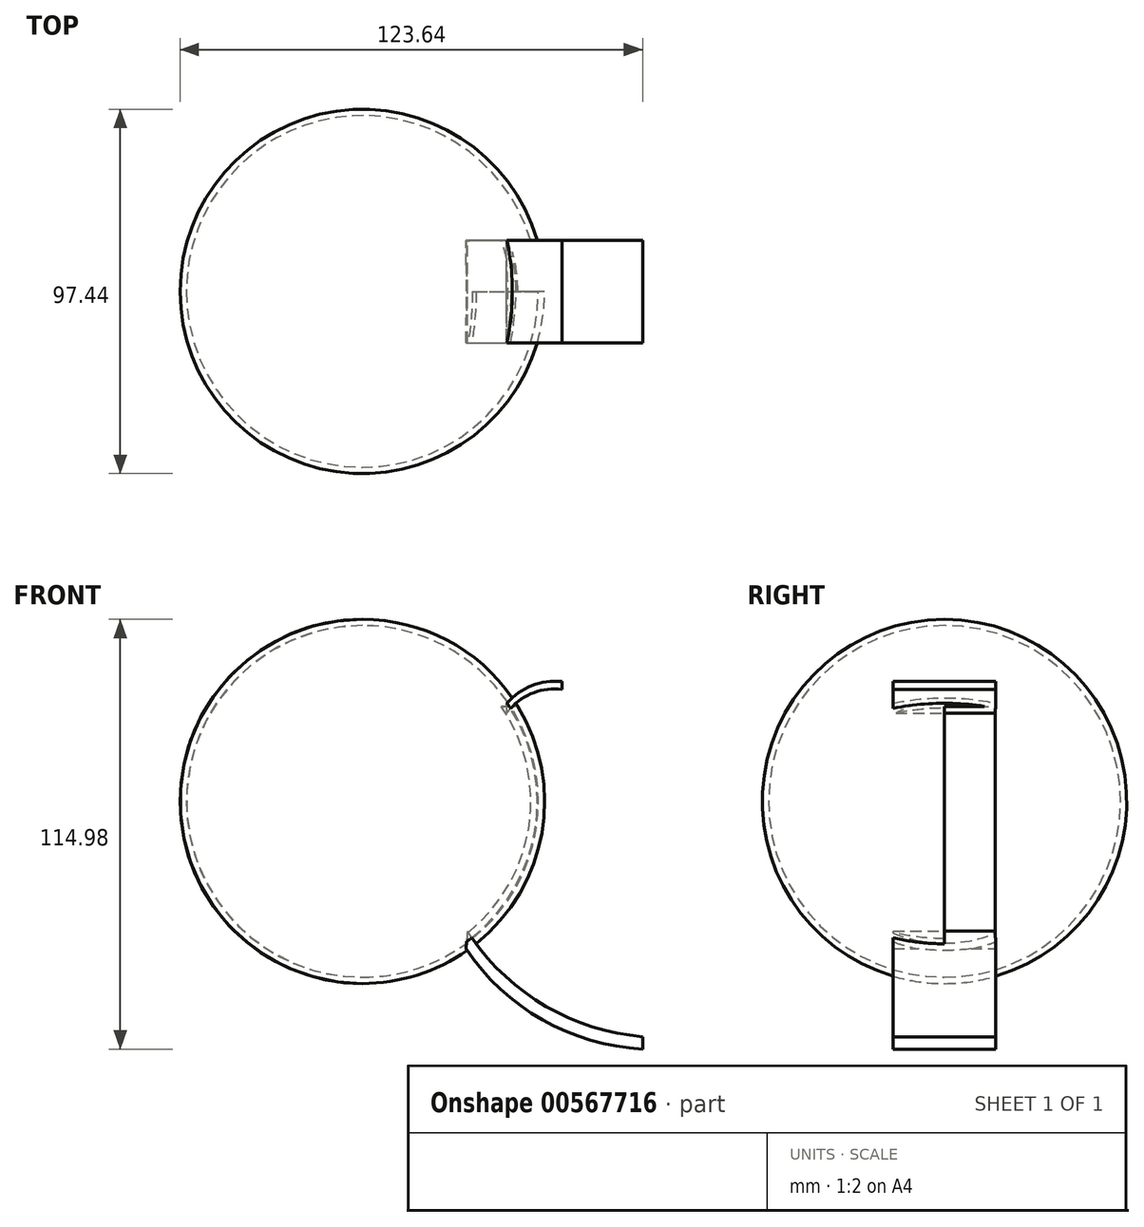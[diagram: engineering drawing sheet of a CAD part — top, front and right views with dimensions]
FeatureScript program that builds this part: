
annotation { "Feature Type Name" : "Feature", "Feature Type Description" : "" }
export const myFeature = defineFeature(function(context is Context, id is Id, definition is map)
    precondition{}
    {
        {
            var Q0;
            Q0=qCreatedBy(makeId("Front.planeOp"),FACE);
            var sketch = newSketch(context, id + "F0", { "sketchPlane" : qUnion([Q0])});
            skLineSegment(sketch, "E0", {"start": v(0, 0) * mm, "end": v(0, 97.44) * mm});
            skArc(sketch, "E1", {"start": v(0, 0) * mm, "mid": v(48.72, 48.72) * mm, "end": v(0, 97.44) * mm});
            skArc(sketch, "E2", {"start": v(0, 4.64) * mm, "mid": v(-1.9, 4.69) * mm, "end": v(-3.78, 4.8) * mm});
            skArc(sketch, "E3", {"start": v(0, 1.68) * mm, "mid": v(47.04, 48.72) * mm, "end": v(0, 95.76) * mm});
            skSolve(sketch);
        }
        {
            var Q0;
            {var subQ0=sQuery(id+"F0.wireOp",EDGE,"E1");Q0=makeQuery(id+"F0.imprint","IMPRINT",FACE,{"disambiguationData":[TD([[makeQuery(id+"F0.imprint","IMPRINT",EDGE,{"derivedFrom":subQ0}),1.0]])]});}
            var Q1;
            Q1=sQuery(id+"F0.wireOp",EDGE,"E0");
            revolve(context, id + "F1", {"entities" : qUnion([Q0]), "axis" : qUnion([Q1]), "revolveType" : RevolveType.ONE_DIRECTION, "angle" : 180 * degree});
        }
        {
            var Q0;
            Q0=makeQuery(id+"F1.opRevolve","SWEPT_BODY",BODY,{"disambiguationData":[OSD([sQuery(id+"F0.wireOp",EDGE,"E0"),sQuery(id+"F0.wireOp",EDGE,"E1"),sQuery(id+"F0.wireOp",EDGE,"E3")])]});
            var Q1;
            Q1=qCreatedBy(makeId("Front.planeOp"),FACE);
            mirror(context, id + "F2", {"operationType" : NewBodyOperationType.ADD, "entities" : qUnion([Q0]), "mirrorPlane" : qUnion([Q1])});
        }
        {
            var Q0;
            Q0=qCreatedBy(makeId("Top.planeOp"),FACE);
            var sketch = newSketch(context, id + "F3", { "sketchPlane" : qUnion([Q0])});
            skLineSegment(sketch, "E4", {"start": v(28.32, 0) * mm, "end": v(28.32, 13.61) * mm});
            skLineSegment(sketch, "E5", {"start": v(28.32, 13.61) * mm, "end": v(62.18, 13.61) * mm});
            skLineSegment(sketch, "E6", {"start": v(62.18, 13.61) * mm, "end": v(62.18, 0) * mm});
            skLineSegment(sketch, "E7", {"start": v(62.18, 0) * mm, "end": v(28.32, 0) * mm});
            skSolve(sketch);
        }
        {
            var Q0;
            Q0=makeQuery(id+"Fv1a8QCHK5ZU15p_1.1.F3.imprint","IMPRINT",FACE,{"disambiguationData":[TD([[makeQuery(id+"Fv1a8QCHK5ZU15p_1.1.F3.imprint","IMPRINT",EDGE,{"derivedFrom":sQuery(id+"Fv1a8QCHK5ZU15p_1.1.F3.wireOp",EDGE,"E4")}),-1.0]])]});
            var Q1;
            Q1=makeQuery(id+"F3.imprint","IMPRINT",FACE,{"disambiguationData":[TD([[makeQuery(id+"F3.imprint","IMPRINT",EDGE,{"derivedFrom":sQuery(id+"F3.wireOp",EDGE,"E4")}),-1.0]])]});
            extrude(context, id + "F4", {"entities" : qUnion([Q0, Q1]), "operationType" : NewBodyOperationType.REMOVE, "depth" : 74.17 * mm, "offsetDistance" : 25.4 * mm});
        }
        {
            var Q0;
            Q0=qCreatedBy(makeId("Front.planeOp"),FACE);
            var sketch = newSketch(context, id + "F5", { "sketchPlane" : qUnion([Q0])});
            skArc(sketch, "E8", {"start": v(28.06, 14) * mm, "mid": v(48.2, -5.57) * mm, "end": v(74.92, -14.22) * mm});
            skArc(sketch, "E9", {"start": v(27.72, 9.28) * mm, "mid": v(48.15, -9.72) * mm, "end": v(74.92, -17.54) * mm});
            skLineSegment(sketch, "E10", {"start": v(28.06, 14) * mm, "end": v(27.72, 9.28) * mm});
            skLineSegment(sketch, "E11", {"start": v(74.92, -14.22) * mm, "end": v(74.92, -17.54) * mm});
            skSolve(sketch);
        }
        {
            var Q0;
            Q0=makeQuery(id+"F5.imprint","IMPRINT",FACE,{"disambiguationData":[TD([[makeQuery(id+"F5.imprint","IMPRINT",EDGE,{"derivedFrom":sQuery(id+"F5.wireOp",EDGE,"E8")}),-1.0]])]});
            extrude(context, id + "F6", {"entities" : qUnion([Q0]), "operationType" : NewBodyOperationType.ADD, "depth" : 13.72 * mm, "offsetDistance" : 25.4 * mm, "hasSecondDirection" : true, "secondDirectionOppositeDirection" : true, "secondDirectionDepth" : 13.72 * mm});
        }
        {
            var Q0;
            Q0=qCreatedBy(makeId("Front.planeOp"),FACE);
            var sketch = newSketch(context, id + "F7", { "sketchPlane" : qUnion([Q0])});
            skArc(sketch, "E12", {"start": v(53.36, 78.67) * mm, "mid": v(45.09, 77.53) * mm, "end": v(38.57, 72.3) * mm});
            skArc(sketch, "E13", {"start": v(53.36, 80.79) * mm, "mid": v(45.21, 79.67) * mm, "end": v(38.57, 74.82) * mm});
            skLineSegment(sketch, "E14", {"start": v(53.36, 80.79) * mm, "end": v(53.36, 78.67) * mm});
            skLineSegment(sketch, "E15", {"start": v(38.57, 74.82) * mm, "end": v(38.57, 72.3) * mm});
            skSolve(sketch);
        }
        {
            var Q0;
            Q0=makeQuery(id+"F7.imprint","IMPRINT",FACE,{"disambiguationData":[TD([[makeQuery(id+"F7.imprint","IMPRINT",EDGE,{"derivedFrom":sQuery(id+"F7.wireOp",EDGE,"E12")}),-1.0]])]});
            extrude(context, id + "F8", {"entities" : qUnion([Q0]), "operationType" : NewBodyOperationType.ADD, "depth" : 13.72 * mm, "offsetDistance" : 25.4 * mm, "hasSecondDirection" : true, "secondDirectionOppositeDirection" : true, "secondDirectionDepth" : 13.72 * mm});
        }
        {
            var Q0;
            Q0=qCreatedBy(makeId("Front.planeOp"),FACE);
            var sketch = newSketch(context, id + "F9", { "sketchPlane" : qUnion([Q0])});
            skLineSegment(sketch, "E16", {"start": v(0, 0) * mm, "end": v(0, 74.99) * mm});
            skSolve(sketch);
        }
        {
            var Q0;
            Q0=makeQuery(id+"F1.opRevolve","SWEPT_BODY",BODY,{"disambiguationData":[OSD([sQuery(id+"F0.wireOp",EDGE,"E0"),sQuery(id+"F0.wireOp",EDGE,"E1"),sQuery(id+"F0.wireOp",EDGE,"E3")])]});
            var Q1;
            Q1=sQuery(id+"F9.wireOp",EDGE,"E16");
            transform(context, id + "F10", {"entities" : qUnion([Q0]), "transformType" : TransformType.ROTATION, "transformAxis" : qUnion([Q1]), "angle" : 40 * degree, "makeCopy" : false});
        }
        {
            var Q0;
            Q0=makeQuery(id+"F1.opRevolve","SWEPT_BODY",BODY,{"disambiguationData":[OSD([sQuery(id+"F0.wireOp",EDGE,"E0"),sQuery(id+"F0.wireOp",EDGE,"E1"),sQuery(id+"F0.wireOp",EDGE,"E3")])]});
            var Q1;
            Q1=sQuery(id+"F9.wireOp",EDGE,"E16");
            transform(context, id + "F11", {"entities" : qUnion([Q0]), "transformType" : TransformType.ROTATION, "transformAxis" : qUnion([Q1]), "angle" : 40 * degree, "oppositeDirection" : true, "makeCopy" : false});
        }
    });
